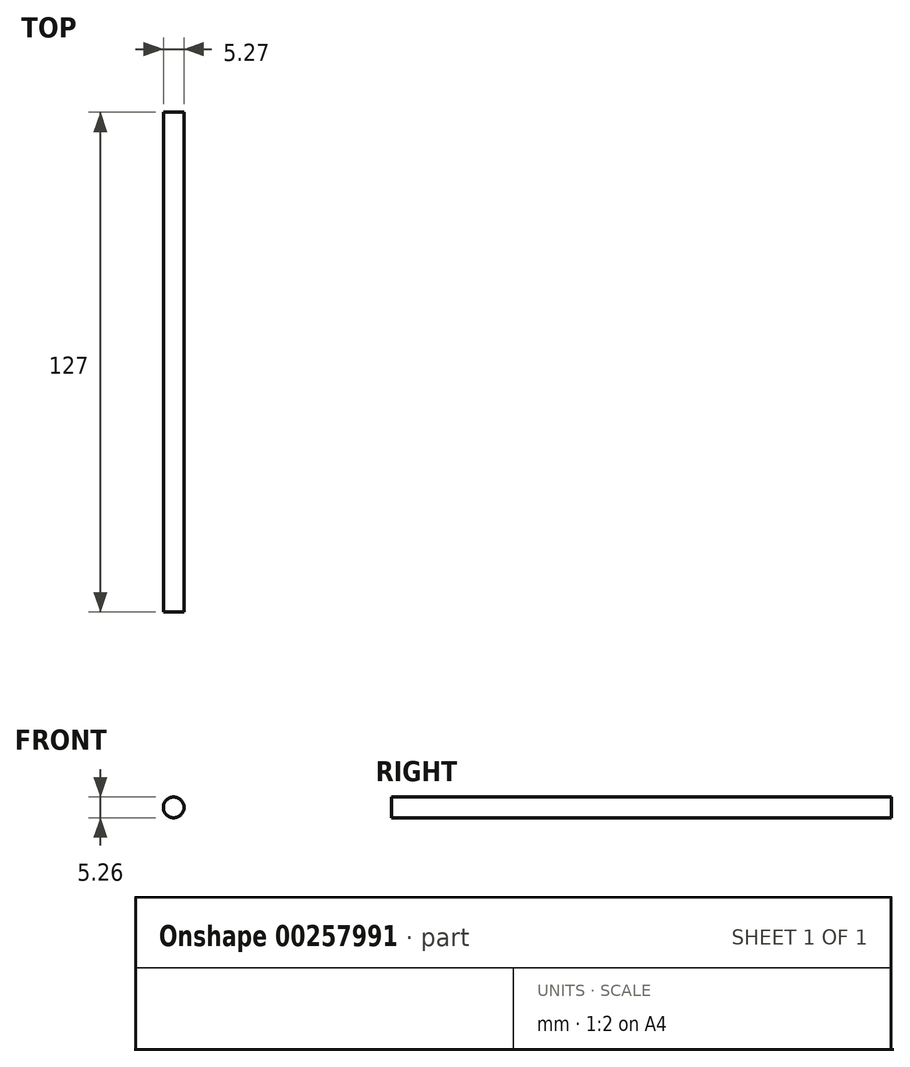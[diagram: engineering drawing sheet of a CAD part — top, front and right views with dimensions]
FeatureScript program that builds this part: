
annotation { "Feature Type Name" : "Feature", "Feature Type Description" : "" }
export const myFeature = defineFeature(function(context is Context, id is Id, definition is map)
    precondition{}
    {
        {
            var Q0;
            Q0=qCreatedBy(makeId("Front.planeOp"),FACE);
            var sketch = newSketch(context, id + "F0", { "sketchPlane" : qUnion([Q0])});
            skCircle(sketch, "E0", {"center": v(-37.12, 43.12) * mm, "radius": 2.63 * mm});
            skSolve(sketch);
        }
        {
            var Q0;
            Q0=makeQuery(id+"F0.imprint","IMPRINT",FACE,{"disambiguationData":[TD([[makeQuery(id+"F0.imprint","IMPRINT",EDGE,{"derivedFrom":sQuery(id+"F0.wireOp",EDGE,"E0")}),1.0]])]});
            extrude(context, id + "F1", {"entities" : qUnion([Q0]), "depth" : 127 * mm});
        }
    });
